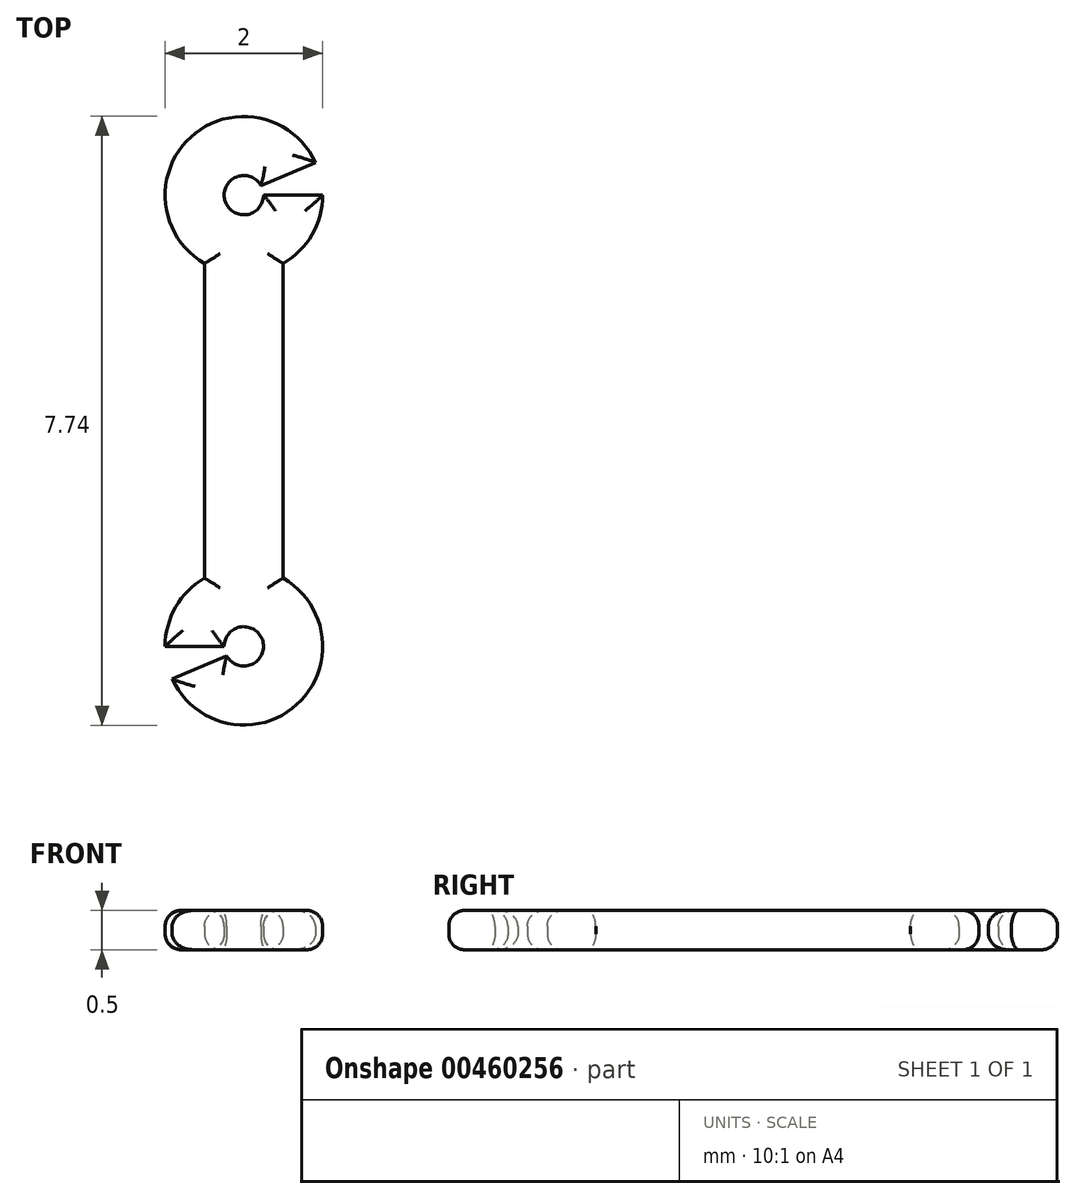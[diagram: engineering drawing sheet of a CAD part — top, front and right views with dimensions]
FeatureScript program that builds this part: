
annotation { "Feature Type Name" : "Feature", "Feature Type Description" : "" }
export const myFeature = defineFeature(function(context is Context, id is Id, definition is map)
    precondition{}
    {
        {
            var Q0;
            Q0=qCreatedBy(makeId("Top.planeOp"),FACE);
            var sketch = newSketch(context, id + "F0", { "sketchPlane" : qUnion([Q0])});
            skArc(sketch, "E0", {"start": v(0.9, 3.28) * mm, "mid": v(-0.67, 3.6) * mm, "end": v(-0.5, 2) * mm});
            skArc(sketch, "E1.MirrorC", {"start": v(0.5, -2) * mm, "mid": v(0.67, -3.6) * mm, "end": v(-0.9, -3.28) * mm});
            skLineSegment(sketch, "E2", {"start": v(0.5, 2) * mm, "end": v(0.5, -2) * mm});
            skLineSegment(sketch, "E3.MirrorCS", {"start": v(-0.5, 2) * mm, "end": v(-0.5, -2) * mm});
            skArc(sketch, "E4", {"start": v(0.22, 3) * mm, "mid": v(-0.24, 2.8) * mm, "end": v(0.25, 2.87) * mm});
            skLineSegment(sketch, "E5", {"start": v(0.25, 2.87) * mm, "end": v(1, 2.87) * mm});
            skLineSegment(sketch, "E6", {"start": v(0.22, 3) * mm, "end": v(0.9, 3.28) * mm});
            skArc(sketch, "E7.trimOffspring", {"start": v(0.5, 2) * mm, "mid": v(0.87, 2.37) * mm, "end": v(1, 2.87) * mm});
            skLineSegment(sketch, "E8.MirrorCS", {"start": v(-0.25, -2.87) * mm, "end": v(-1, -2.87) * mm});
            skLineSegment(sketch, "E9.MirrorCS", {"start": v(-0.22, -3) * mm, "end": v(-0.9, -3.28) * mm});
            skArc(sketch, "E10", {"start": v(-0.22, -3) * mm, "mid": v(0.24, -2.8) * mm, "end": v(-0.25, -2.87) * mm});
            skArc(sketch, "E11.trimOffspring", {"start": v(-1, -2.87) * mm, "mid": v(-0.87, -2.37) * mm, "end": v(-0.5, -2) * mm});
            skSolve(sketch);
        }
        {
            var Q0;
            Q0=makeQuery(id+"F0.imprint","IMPRINT",FACE,{"disambiguationData":[TD([[makeQuery(id+"F0.imprint","IMPRINT",EDGE,{"derivedFrom":sQuery(id+"F0.wireOp",EDGE,"E0")}),1.0]])]});
            extrude(context, id + "F1", {"entities" : qUnion([Q0]), "depth" : 0.5 * mm});
        }
        {
            var Q0;
            Q0=makeQuery(id+"F1.opExtrude","CAP_FACE",FACE,{"disambiguationData":[OSD([sQuery(id+"F0.wireOp",EDGE,"E0"),sQuery(id+"F0.wireOp",EDGE,"E1.MirrorC"),sQuery(id+"F0.wireOp",EDGE,"E2"),sQuery(id+"F0.wireOp",EDGE,"E3.MirrorCS"),sQuery(id+"F0.wireOp",EDGE,"E4"),sQuery(id+"F0.wireOp",EDGE,"E5"),sQuery(id+"F0.wireOp",EDGE,"E6"),sQuery(id+"F0.wireOp",EDGE,"E7.trimOffspring"),sQuery(id+"F0.wireOp",EDGE,"E8.MirrorCS"),sQuery(id+"F0.wireOp",EDGE,"E9.MirrorCS"),sQuery(id+"F0.wireOp",EDGE,"E10"),sQuery(id+"F0.wireOp",EDGE,"E11.trimOffspring")])],"isStart":true});
            fillet(context, id + "F2", {"entities" : qUnion([Q0]), "radius" : 0.2 * mm, "tangentPropagation" : true, "allowEdgeOverflow" : false});
        }
        {
            var Q0;
            Q0=makeQuery(id+"F1.opExtrude","CAP_FACE",FACE,{"disambiguationData":[OSD([sQuery(id+"F0.wireOp",EDGE,"E0"),sQuery(id+"F0.wireOp",EDGE,"E1.MirrorC"),sQuery(id+"F0.wireOp",EDGE,"E2"),sQuery(id+"F0.wireOp",EDGE,"E3.MirrorCS"),sQuery(id+"F0.wireOp",EDGE,"E4"),sQuery(id+"F0.wireOp",EDGE,"E5"),sQuery(id+"F0.wireOp",EDGE,"E6"),sQuery(id+"F0.wireOp",EDGE,"E7.trimOffspring"),sQuery(id+"F0.wireOp",EDGE,"E8.MirrorCS"),sQuery(id+"F0.wireOp",EDGE,"E9.MirrorCS"),sQuery(id+"F0.wireOp",EDGE,"E10"),sQuery(id+"F0.wireOp",EDGE,"E11.trimOffspring")])],"isStart":false});
            fillet(context, id + "F3", {"entities" : qUnion([Q0]), "radius" : 0.2 * mm, "tangentPropagation" : true, "allowEdgeOverflow" : false});
        }
    });
